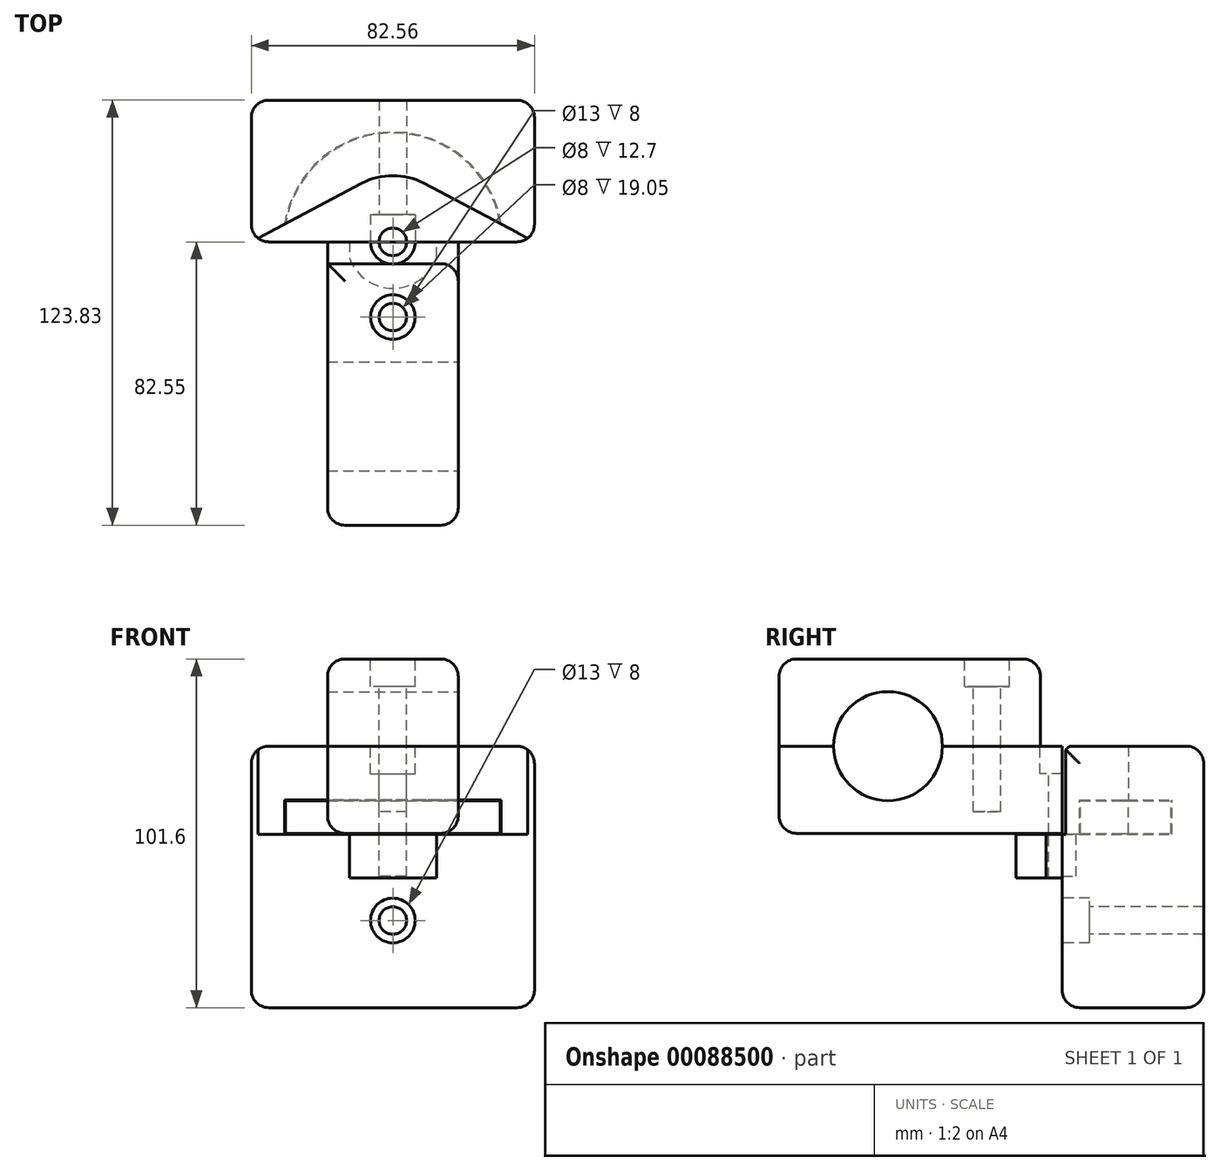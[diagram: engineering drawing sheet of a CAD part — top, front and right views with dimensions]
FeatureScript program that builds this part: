
annotation { "Feature Type Name" : "Feature", "Feature Type Description" : "" }
export const myFeature = defineFeature(function(context is Context, id is Id, definition is map)
    precondition{}
    {
        {
            var Q0;
            Q0=qCreatedBy(makeId("Top.planeOp"),FACE);
            var sketch = newSketch(context, id + "F0", { "sketchPlane" : qUnion([Q0])});
            skLineSegment(sketch, "E0.bottom", {"start": v(0, 0) * mm, "end": v(38.1, 0) * mm});
            skLineSegment(sketch, "E0.top", {"start": v(0, 82.55) * mm, "end": v(38.1, 82.55) * mm});
            skLineSegment(sketch, "E0.left", {"start": v(0, 0) * mm, "end": v(0, 82.55) * mm});
            skLineSegment(sketch, "E0.right", {"start": v(38.1, 0) * mm, "end": v(38.1, 82.55) * mm});
            skArc(sketch, "E1", {"start": v(38.1, 82.55) * mm, "mid": v(19.05, 101.6) * mm, "end": v(0, 82.55) * mm});
            skSolve(sketch);
        }
        {
            var Q0;
            Q0=makeQuery(id+"F0.imprint","IMPRINT",FACE,{"disambiguationData":[TD([[makeQuery(id+"F0.imprint","IMPRINT",EDGE,{"derivedFrom":sQuery(id+"F0.wireOp",EDGE,"E0.bottom")}),1.0]])]});
            var Q1;
            Q1=makeQuery(id+"F0.imprint","IMPRINT",FACE,{"disambiguationData":[TD([[makeQuery(id+"F0.imprint","IMPRINT",EDGE,{"derivedFrom":sQuery(id+"F0.wireOp",EDGE,"E0.top")}),1.0]])]});
            extrude(context, id + "F1", {"entities" : qUnion([Q0, Q1]), "depth" : 25.4 * mm});
        }
        {
            var Q0;
            Q0=makeQuery(id+"F1.opExtrude","SWEPT_FACE",FACE,{"disambiguationData":[OSD([sQuery(id+"F0.wireOp",EDGE,"E0.right")])]});
            var sketch = newSketch(context, id + "F2", { "sketchPlane" : qUnion([Q0])});
            skCircle(sketch, "E2", {"center": v(31.75, 25.4) * mm, "radius": 15.88 * mm});
            skSolve(sketch);
        }
        {
            var Q0;
            {var subQ0=sQuery(id+"F2.wireOp",EDGE,"E2");var subQ1=makeQuery(id+"F1.opExtrude","CAP_EDGE",EDGE,{"disambiguationData":[OSD([sQuery(id+"F0.wireOp",EDGE,"E0.right")])],"isStart":false});var subQ2=makeQuery(id+"F2.imprint","INTERSECT",VERTEX,{"disambiguationData":[OD(0.0)],"derivedFrom":[subQ1,subQ0]});Q0=makeQuery(id+"F2.imprint","IMPRINT",FACE,{"disambiguationData":[TD([[makeQuery(id+"F2.imprint","IMPRINT",EDGE,{"disambiguationData":[TD([[subQ2,-1.0]])],"derivedFrom":subQ0}),1.0]])]});}
            extrude(context, id + "F3", {"entities" : qUnion([Q0]), "operationType" : NewBodyOperationType.REMOVE, "endBound" : BoundingType.THROUGH_ALL, "oppositeDirection" : true, "depth" : 25.4 * mm});
        }
        {
            var Q0;
            Q0=makeQuery(id+"F1.opExtrude","SWEPT_EDGE",EDGE,{"disambiguationData":[OSD([sQuery(id+"F0.wireOp",EDGE,"E0.top"),sQuery(id+"F0.wireOp",EDGE,"E0.right"),sQuery(id+"F0.wireOp",EDGE,"E1")])]});
            var Q1;
            Q1=makeQuery(id+"F1.opExtrude","SWEPT_EDGE",EDGE,{"disambiguationData":[OSD([sQuery(id+"F0.wireOp",EDGE,"E0.top"),sQuery(id+"F0.wireOp",EDGE,"E0.left"),sQuery(id+"F0.wireOp",EDGE,"E1")])]});
            cPlane(context, id + "F4", {"entities" : qUnion([Q0, Q1]), "cplaneType" : CPlaneType.LINE_ANGLE, "offset" : 152.4 * mm, "angle" : 0 * degree, "width" : 152.4 * mm, "height" : 152.4 * mm});
        }
        {
            var Q0;
            Q0=qCreatedBy(id+"F4.planeOp",FACE);
            var sketch = newSketch(context, id + "F5", { "sketchPlane" : qUnion([Q0])});
            skLineSegment(sketch, "E3.0", {"start": v(-38.1, 25.4) * mm, "end": v(-38.1, 0) * mm});
            skLineSegment(sketch, "E4.bottom", {"start": v(-38.1, 0) * mm, "end": v(-50.8, 0) * mm});
            skLineSegment(sketch, "E4.top", {"start": v(-38.1, 9.53) * mm, "end": v(-50.8, 9.53) * mm});
            skLineSegment(sketch, "E4.left", {"start": v(-38.1, 0) * mm, "end": v(-38.1, 9.53) * mm});
            skLineSegment(sketch, "E4.right", {"start": v(-50.8, 0) * mm, "end": v(-50.8, 9.53) * mm});
            skSolve(sketch);
        }
        {
            var Q0;
            Q0=makeQuery(id+"F5.imprint","IMPRINT",FACE,{"disambiguationData":[TD([[makeQuery(id+"F5.imprint","IMPRINT",EDGE,{"derivedFrom":sQuery(id+"F5.wireOp",EDGE,"E4.bottom")}),-1.0]])]});
            var Q1;
            Q1=makeQuery(id+"F1.opExtrude","CAP_EDGE",EDGE,{"disambiguationData":[OSD([sQuery(id+"F0.wireOp",EDGE,"E1")])],"isStart":false});
            sweep(context, id + "F6", {"operationType" : NewBodyOperationType.ADD, "profiles" : qUnion([Q0]), "path" : qUnion([Q1])});
        }
        {
            var Q0;
            {var subQ0=sQuery(id+"F0.wireOp",EDGE,"E0.left");var subQ1=sQuery(id+"F0.wireOp",EDGE,"E0.right");var subQ2=sQuery(id+"F0.wireOp",EDGE,"E1");Q0=makeQuery(id+"F3.boolean.opBoolean","SPLIT",FACE,{"disambiguationData":[TD([makeQuery(id+"F1.opExtrude","SWEPT_FACE",FACE,{"disambiguationData":[OSD([subQ2])]})])],"derivedFrom":makeQuery(id+"F1.opExtrude","CAP_FACE",FACE,{"disambiguationData":[OSD([sQuery(id+"F0.wireOp",EDGE,"E0.bottom"),subQ0,subQ1,subQ2])],"isStart":false})});}
            var sketch = newSketch(context, id + "F7", { "sketchPlane" : qUnion([Q0])});
            skLineSegment(sketch, "E5.bottom", {"start": v(19.05, 82.55) * mm, "end": v(-22.23, 82.55) * mm});
            skLineSegment(sketch, "E5.top", {"start": v(19.05, 123.83) * mm, "end": v(-22.23, 123.83) * mm});
            skLineSegment(sketch, "E5.left", {"start": v(19.05, 82.55) * mm, "end": v(19.05, 123.83) * mm});
            skLineSegment(sketch, "E5.right", {"start": v(-22.23, 82.55) * mm, "end": v(-22.23, 123.83) * mm});
            skLineSegment(sketch, "E6.MirrorCS", {"start": v(19.05, 123.83) * mm, "end": v(60.32, 123.83) * mm});
            skLineSegment(sketch, "E7.MirrorCS", {"start": v(60.32, 82.55) * mm, "end": v(60.32, 123.83) * mm});
            skLineSegment(sketch, "E8.MirrorCS", {"start": v(19.05, 82.55) * mm, "end": v(60.32, 82.55) * mm});
            skSolve(sketch);
        }
        {
            var Q0;
            {var subQ1=sQuery(id+"F0.wireOp",EDGE,"E1");var subQ3=makeQuery(id+"F1.opExtrude","CAP_EDGE",EDGE,{"disambiguationData":[OSD([subQ1])],"isStart":false});var subQ5=sQuery(id+"F7.wireOp",EDGE,"E5.left");var subQ7=makeQuery(id+"F7.imprint","INTERSECT",VERTEX,{"derivedFrom":[subQ3,subQ5]});Q0=makeQuery(id+"F7.imprint","IMPRINT",FACE,{"disambiguationData":[TD([[makeQuery(id+"F7.imprint","IMPRINT",EDGE,{"disambiguationData":[TD([[subQ7,1.0]])],"derivedFrom":subQ5}),1.0]])]});}
            var Q1;
            {var subQ1=sQuery(id+"F7.wireOp",EDGE,"E5.left");var subQ3=sQuery(id+"F0.wireOp",EDGE,"E1");var subQ4=makeQuery(id+"F1.opExtrude","CAP_EDGE",EDGE,{"disambiguationData":[OSD([subQ3])],"isStart":false});var subQ5=makeQuery(id+"F7.imprint","INTERSECT",VERTEX,{"derivedFrom":[subQ4,subQ1]});Q1=makeQuery(id+"F7.imprint","IMPRINT",FACE,{"disambiguationData":[TD([[makeQuery(id+"F7.imprint","IMPRINT",EDGE,{"disambiguationData":[TD([[subQ5,1.0]])],"derivedFrom":subQ1}),-1.0]])]});}
            var Q2;
            {var subQ6=sQuery(id+"F7.wireOp",EDGE,"E6.MirrorCS");Q2=makeQuery(id+"F7.imprint","IMPRINT",FACE,{"disambiguationData":[TD([[makeQuery(id+"F7.imprint","IMPRINT",EDGE,{"derivedFrom":subQ6}),-1.0]])]});}
            var Q3;
            {var subQ2=sQuery(id+"F7.wireOp",EDGE,"E5.top");Q3=makeQuery(id+"F7.imprint","IMPRINT",FACE,{"disambiguationData":[TD([[makeQuery(id+"F7.imprint","IMPRINT",EDGE,{"derivedFrom":subQ2}),1.0]])]});}
            extrude(context, id + "F8", {"entities" : qUnion([Q0, Q1, Q2, Q3]), "oppositeDirection" : true, "depth" : 76.2 * mm});
        }
        {
            var Q0;
            Q0=makeQuery(id+"F1.opExtrude","SWEPT_BODY",BODY,{"disambiguationData":[OSD([sQuery(id+"F0.wireOp",EDGE,"E0.bottom"),sQuery(id+"F0.wireOp",EDGE,"E0.left"),sQuery(id+"F0.wireOp",EDGE,"E0.right"),sQuery(id+"F0.wireOp",EDGE,"E1")])]});
            var Q1;
            Q1=makeQuery(id+"F8.opExtrude","SWEPT_BODY",BODY,{"disambiguationData":[OSD([sQuery(id+"F7.wireOp",EDGE,"E5.bottom"),sQuery(id+"F7.wireOp",EDGE,"E5.top"),sQuery(id+"F7.wireOp",EDGE,"E5.right"),sQuery(id+"F7.wireOp",EDGE,"E6.MirrorCS"),sQuery(id+"F7.wireOp",EDGE,"E7.MirrorCS"),sQuery(id+"F7.wireOp",EDGE,"E8.MirrorCS")])]});
            booleanBodies(context, id + "F9", {"operationType" : BooleanOperationType.SUBTRACTION, "tools" : qUnion([Q0]), "targets" : qUnion([Q1]), "offset" : true, "offsetAll" : true, "offsetDistance" : 0.25 * mm, "keepTools" : true});
        }
        {
            var Q0;
            Q0=makeQuery(id+"F8.opExtrude","CAP_FACE",FACE,{"disambiguationData":[OSD([sQuery(id+"F7.wireOp",EDGE,"E5.bottom"),sQuery(id+"F7.wireOp",EDGE,"E5.top"),sQuery(id+"F7.wireOp",EDGE,"E5.right"),sQuery(id+"F7.wireOp",EDGE,"E6.MirrorCS"),sQuery(id+"F7.wireOp",EDGE,"E7.MirrorCS"),sQuery(id+"F7.wireOp",EDGE,"E8.MirrorCS")])],"isStart":true});
            var sketch = newSketch(context, id + "F10", { "sketchPlane" : qUnion([Q0])});
            skLineSegment(sketch, "E9", {"start": v(60.32, 82.55) * mm, "end": v(28.08, 99.61) * mm});
            skLineSegment(sketch, "E10", {"start": v(-22.23, 82.55) * mm, "end": v(10.02, 99.61) * mm});
            skLineSegment(sketch, "E11", {"start": v(-22.23, 82.55) * mm, "end": v(60.32, 82.55) * mm});
            skArc(sketch, "E12.0", {"start": v(-0.25, 82.55) * mm, "mid": v(19.05, 101.85) * mm, "end": v(38.35, 82.55) * mm});
            skSolve(sketch);
        }
        {
            var Q0;
            Q0 = qSketchRegion(id + "F10", true);
            var Q1;
            {var subQ0=sQuery(id+"F0.wireOp",EDGE,"E1");Q1=makeQuery(id+"F9.tempBoolean.opBoolean","COPY",FACE,{"derivedFrom":makeQuery(id+"F9.offsetTempBody.opPattern","COPY",FACE,{"derivedFrom":makeQuery(id+"F6.boolean.opBoolean","MERGE",FACE,{"derivedFrom":[makeQuery(id+"F1.opExtrude","CAP_FACE",FACE,{"disambiguationData":[OSD([sQuery(id+"F0.wireOp",EDGE,"E0.bottom"),sQuery(id+"F0.wireOp",EDGE,"E0.left"),sQuery(id+"F0.wireOp",EDGE,"E0.right"),subQ0])],"isStart":true}),makeQuery(id+"F6.opSweep","SWEPT_FACE",FACE,{"disambiguationData":[OSD([subQ0,sQuery(id+"F5.wireOp",EDGE,"E4.bottom")])]})]}),"instanceName":"1"})});}
            extrude(context, id + "F11", {"entities" : qUnion([Q0]), "operationType" : NewBodyOperationType.REMOVE, "endBound" : BoundingType.UP_TO_SURFACE, "oppositeDirection" : true, "endBoundEntityFace" : qUnion([Q1]), "depth" : 25.4 * mm});
        }
        {
            var Q0;
            Q0=makeQuery(id+"F11.boolean.opBoolean","COPY",FACE,{"derivedFrom":makeQuery(id+"F11.opExtrude","SWEPT_FACE",FACE,{"disambiguationData":[OSD([sQuery(id+"F10.wireOp",EDGE,"E9")])]})});
            var sketch = newSketch(context, id + "F12", { "sketchPlane" : qUnion([Q0])});
            skCircle(sketch, "E13", {"center": v(29.03, 25.4) * mm, "radius": 15.88 * mm});
            skSolve(sketch);
        }
        {
            var Q0;
            {var subQ0=sQuery(id+"F12.wireOp",EDGE,"E13");var subQ1=sQuery(id+"F10.wireOp",EDGE,"E9");var subQ5=makeQuery(id+"F11.boolean.opBoolean","COPY",EDGE,{"derivedFrom":makeQuery(id+"F11.opExtrude","CAP_EDGE",EDGE,{"disambiguationData":[OSD([subQ1])],"isStart":true})});var subQ6=makeQuery(id+"F12.imprint","INTERSECT",VERTEX,{"derivedFrom":[subQ5,subQ0]});Q0=makeQuery(id+"F12.imprint","IMPRINT",FACE,{"disambiguationData":[TD([[makeQuery(id+"F12.imprint","IMPRINT",EDGE,{"disambiguationData":[TD([[subQ6,-1.0]])],"derivedFrom":subQ0}),1.0]])]});}
            extrude(context, id + "F13", {"entities" : qUnion([Q0]), "operationType" : NewBodyOperationType.REMOVE, "oppositeDirection" : true, "depth" : 25.4 * mm});
        }
        {
            var Q0;
            Q0=makeQuery(id+"F11.boolean.opBoolean","COPY",FACE,{"derivedFrom":makeQuery(id+"F11.opExtrude","SWEPT_FACE",FACE,{"disambiguationData":[OSD([sQuery(id+"F10.wireOp",EDGE,"E10")])]})});
            var sketch = newSketch(context, id + "F14", { "sketchPlane" : qUnion([Q0])});
            skCircle(sketch, "E14", {"center": v(4.65, 25.4) * mm, "radius": 15.88 * mm});
            skSolve(sketch);
        }
        {
            var Q0;
            {var subQ0=sQuery(id+"F14.wireOp",EDGE,"E14");var subQ1=sQuery(id+"F10.wireOp",EDGE,"E10");var subQ5=makeQuery(id+"F11.boolean.opBoolean","COPY",EDGE,{"derivedFrom":makeQuery(id+"F11.opExtrude","CAP_EDGE",EDGE,{"disambiguationData":[OSD([subQ1])],"isStart":true})});var subQ6=makeQuery(id+"F14.imprint","INTERSECT",VERTEX,{"derivedFrom":[subQ5,subQ0]});Q0=makeQuery(id+"F14.imprint","IMPRINT",FACE,{"disambiguationData":[TD([[makeQuery(id+"F14.imprint","IMPRINT",EDGE,{"disambiguationData":[TD([[subQ6,1.0]])],"derivedFrom":subQ0}),1.0]])]});}
            extrude(context, id + "F15", {"entities" : qUnion([Q0]), "operationType" : NewBodyOperationType.REMOVE, "oppositeDirection" : true, "depth" : 25.4 * mm});
        }
        {
            var Q0;
            Q0=makeQuery(id+"F8.opExtrude","SWEPT_FACE",FACE,{"disambiguationData":[OSD([sQuery(id+"F7.wireOp",EDGE,"E5.bottom"),sQuery(id+"F7.wireOp",EDGE,"E8.MirrorCS")])]});
            var sketch = newSketch(context, id + "F16", { "sketchPlane" : qUnion([Q0])});
            skCircle(sketch, "E15", {"center": v(19.05, -25.4) * mm, "radius": 4 * mm});
            skPoint(sketch, "E15.centerSnap0", {"position": v(19.05, -50.8) * mm});
            skSolve(sketch);
        }
        {
            var Q0;
            Q0=makeQuery(id+"F16.imprint","IMPRINT",FACE,{"disambiguationData":[TD([[makeQuery(id+"F16.imprint","IMPRINT",EDGE,{"derivedFrom":sQuery(id+"F16.wireOp",EDGE,"E15")}),1.0]])]});
            extrude(context, id + "F17", {"entities" : qUnion([Q0]), "operationType" : NewBodyOperationType.REMOVE, "endBound" : BoundingType.THROUGH_ALL, "oppositeDirection" : true, "depth" : 25.4 * mm});
        }
        {
            var Q0;
            Q0=makeQuery(id+"F8.opExtrude","SWEPT_FACE",FACE,{"disambiguationData":[OSD([sQuery(id+"F7.wireOp",EDGE,"E5.bottom"),sQuery(id+"F7.wireOp",EDGE,"E8.MirrorCS")])]});
            var sketch = newSketch(context, id + "F18", { "sketchPlane" : qUnion([Q0])});
            skCircle(sketch, "E16.0", {"center": v(19.05, -25.4) * mm, "radius": 6.5 * mm});
            skSolve(sketch);
        }
        {
            var Q0;
            Q0=makeQuery(id+"F18.imprint","IMPRINT",FACE,{"disambiguationData":[TD([[makeQuery(id+"F18.imprint","IMPRINT",EDGE,{"derivedFrom":sQuery(id+"F18.wireOp",EDGE,"E16.0")}),1.0]])]});
            extrude(context, id + "F19", {"entities" : qUnion([Q0]), "operationType" : NewBodyOperationType.REMOVE, "oppositeDirection" : true, "depth" : 8 * mm});
        }
        {
            var Q0;
            Q0=makeQuery(id+"F1.opExtrude","SWEPT_FACE",FACE,{"disambiguationData":[OSD([sQuery(id+"F0.wireOp",EDGE,"E0.right")])]});
            var sketch = newSketch(context, id + "F20", { "sketchPlane" : qUnion([Q0])});
            skArc(sketch, "E17.0.0", {"start": v(47.62, 25.4) * mm, "mid": v(31.75, 9.53) * mm, "end": v(15.87, 25.4) * mm});
            skLineSegment(sketch, "E17.0.1", {"start": v(15.87, 25.4) * mm, "end": v(0, 25.4) * mm});
            skLineSegment(sketch, "E17.0.2", {"start": v(0, 25.4) * mm, "end": v(0, 0) * mm});
            skLineSegment(sketch, "E17.0.3", {"start": v(0, 0) * mm, "end": v(82.55, 0) * mm});
            skLineSegment(sketch, "E17.0.4", {"start": v(82.55, 0) * mm, "end": v(82.55, 9.53) * mm});
            skLineSegment(sketch, "E17.0.5", {"start": v(82.55, 9.53) * mm, "end": v(82.55, 25.4) * mm});
            skLineSegment(sketch, "E17.0.6", {"start": v(82.55, 25.4) * mm, "end": v(47.62, 25.4) * mm});
            skLineSegment(sketch, "E18.bottom", {"start": v(0, 25.4) * mm, "end": v(76.2, 25.4) * mm});
            skLineSegment(sketch, "E18.top", {"start": v(0, 50.8) * mm, "end": v(76.2, 50.8) * mm});
            skLineSegment(sketch, "E18.left", {"start": v(0, 25.4) * mm, "end": v(0, 50.8) * mm});
            skLineSegment(sketch, "E18.right", {"start": v(76.2, 25.4) * mm, "end": v(76.2, 50.8) * mm});
            skArc(sketch, "E19.MirrorCS", {"start": v(47.62, 25.4) * mm, "mid": v(31.75, 41.28) * mm, "end": v(15.87, 25.4) * mm});
            skSolve(sketch);
        }
        {
            var Q0;
            Q0=makeQuery(id+"F20.imprint","IMPRINT",FACE,{"disambiguationData":[TD([[makeQuery(id+"F20.imprint","IMPRINT",EDGE,{"derivedFrom":sQuery(id+"F20.wireOp",EDGE,"E18.top")}),-1.0]])]});
            var Q1;
            Q1=makeQuery(id+"F1.opExtrude","SWEPT_FACE",FACE,{"disambiguationData":[OSD([sQuery(id+"F0.wireOp",EDGE,"E0.left")])]});
            extrude(context, id + "F21", {"entities" : qUnion([Q0]), "endBound" : BoundingType.UP_TO_SURFACE, "oppositeDirection" : true, "endBoundEntityFace" : qUnion([Q1]), "depth" : 25.4 * mm});
        }
        {
            var Q0;
            Q0=makeQuery(id+"F21.opExtrude","SWEPT_FACE",FACE,{"disambiguationData":[OSD([sQuery(id+"F20.wireOp",EDGE,"E18.top")])]});
            var sketch = newSketch(context, id + "F22", { "sketchPlane" : qUnion([Q0])});
            skCircle(sketch, "E20", {"center": v(19.05, 60.62) * mm, "radius": 4 * mm});
            skSolve(sketch);
        }
        {
            var Q0;
            Q0 = qSketchRegion(id + "F22", true);
            extrude(context, id + "F23", {"entities" : qUnion([Q0]), "operationType" : NewBodyOperationType.REMOVE, "oppositeDirection" : true, "depth" : 44.45 * mm});
        }
        {
            var Q0;
            Q0=makeQuery(id+"F21.opExtrude","SWEPT_EDGE",EDGE,{"disambiguationData":[OSD([sQuery(id+"F20.wireOp",EDGE,"E18.top"),sQuery(id+"F20.wireOp",EDGE,"E18.left")])]});
            var Q1;
            Q1=makeQuery(id+"F21.opExtrude","CAP_EDGE",EDGE,{"disambiguationData":[OSD([sQuery(id+"F20.wireOp",EDGE,"E18.top")])],"isStart":true});
            var Q2;
            Q2=makeQuery(id+"F21.opExtrude","CAP_EDGE",EDGE,{"disambiguationData":[OSD([sQuery(id+"F20.wireOp",EDGE,"E18.top")])],"isStart":false});
            var Q3;
            Q3=makeQuery(id+"F21.opExtrude","CAP_EDGE",EDGE,{"disambiguationData":[OSD([sQuery(id+"F20.wireOp",EDGE,"E18.left")])],"isStart":false});
            var Q4;
            Q4=makeQuery(id+"F1.opExtrude","SWEPT_EDGE",EDGE,{"disambiguationData":[OSD([sQuery(id+"F0.wireOp",EDGE,"E0.bottom"),sQuery(id+"F0.wireOp",EDGE,"E0.left")])]});
            var Q5;
            Q5=makeQuery(id+"F1.opExtrude","SWEPT_EDGE",EDGE,{"disambiguationData":[OSD([sQuery(id+"F0.wireOp",EDGE,"E0.bottom"),sQuery(id+"F0.wireOp",EDGE,"E0.right")])]});
            var Q6;
            Q6=makeQuery(id+"F21.opExtrude","CAP_EDGE",EDGE,{"disambiguationData":[OSD([sQuery(id+"F20.wireOp",EDGE,"E18.left")])],"isStart":true});
            var Q7;
            Q7=makeQuery(id+"F21.opExtrude","CAP_EDGE",EDGE,{"disambiguationData":[OSD([sQuery(id+"F20.wireOp",EDGE,"E18.right")])],"isStart":true});
            var Q8;
            Q8=makeQuery(id+"F21.opExtrude","SWEPT_EDGE",EDGE,{"disambiguationData":[OSD([sQuery(id+"F20.wireOp",EDGE,"E18.top"),sQuery(id+"F20.wireOp",EDGE,"E18.right")])]});
            var Q9;
            Q9=makeQuery(id+"F1.opExtrude","CAP_EDGE",EDGE,{"disambiguationData":[OSD([sQuery(id+"F0.wireOp",EDGE,"E0.bottom")])],"isStart":true});
            var Q10;
            Q10=makeQuery(id+"F1.opExtrude","CAP_EDGE",EDGE,{"disambiguationData":[OSD([sQuery(id+"F0.wireOp",EDGE,"E0.right")])],"isStart":true});
            var Q11;
            Q11=makeQuery(id+"F1.opExtrude","CAP_EDGE",EDGE,{"disambiguationData":[OSD([sQuery(id+"F0.wireOp",EDGE,"E0.left")])],"isStart":true});
            var Q12;
            Q12=makeQuery(id+"F8.opExtrude","CAP_EDGE",EDGE,{"disambiguationData":[OSD([sQuery(id+"F7.wireOp",EDGE,"E5.right")])],"isStart":true});
            var Q13;
            Q13=makeQuery(id+"F8.opExtrude","SWEPT_EDGE",EDGE,{"disambiguationData":[OSD([sQuery(id+"F7.wireOp",EDGE,"E5.top"),sQuery(id+"F7.wireOp",EDGE,"E5.right")])]});
            var Q14;
            Q14=makeQuery(id+"F8.opExtrude","CAP_EDGE",EDGE,{"disambiguationData":[OSD([sQuery(id+"F7.wireOp",EDGE,"E5.right")])],"isStart":false});
            var Q15;
            Q15=makeQuery(id+"F11.boolean.opBoolean","SPLIT",EDGE,{"derivedFrom":makeQuery(id+"F8.opExtrude","SWEPT_EDGE",EDGE,{"disambiguationData":[OSD([sQuery(id+"F7.wireOp",EDGE,"E5.bottom"),sQuery(id+"F7.wireOp",EDGE,"E5.right")])]})});
            var Q16;
            Q16=makeQuery(id+"F8.opExtrude","CAP_EDGE",EDGE,{"disambiguationData":[OSD([sQuery(id+"F7.wireOp",EDGE,"E5.bottom"),sQuery(id+"F7.wireOp",EDGE,"E8.MirrorCS")])],"isStart":false});
            var Q17;
            Q17=makeQuery(id+"F8.opExtrude","CAP_EDGE",EDGE,{"disambiguationData":[OSD([sQuery(id+"F7.wireOp",EDGE,"E5.top"),sQuery(id+"F7.wireOp",EDGE,"E6.MirrorCS")])],"isStart":true});
            var Q18;
            Q18=makeQuery(id+"F11.boolean.opBoolean","SPLIT",EDGE,{"derivedFrom":makeQuery(id+"F8.opExtrude","SWEPT_EDGE",EDGE,{"disambiguationData":[OSD([sQuery(id+"F7.wireOp",EDGE,"E7.MirrorCS"),sQuery(id+"F7.wireOp",EDGE,"E8.MirrorCS")])]})});
            var Q19;
            Q19=makeQuery(id+"F8.opExtrude","CAP_EDGE",EDGE,{"disambiguationData":[OSD([sQuery(id+"F7.wireOp",EDGE,"E7.MirrorCS")])],"isStart":false});
            var Q20;
            Q20=makeQuery(id+"F8.opExtrude","SWEPT_EDGE",EDGE,{"disambiguationData":[OSD([sQuery(id+"F7.wireOp",EDGE,"E6.MirrorCS"),sQuery(id+"F7.wireOp",EDGE,"E7.MirrorCS")])]});
            var Q21;
            Q21=makeQuery(id+"F8.opExtrude","CAP_EDGE",EDGE,{"disambiguationData":[OSD([sQuery(id+"F7.wireOp",EDGE,"E5.top"),sQuery(id+"F7.wireOp",EDGE,"E6.MirrorCS")])],"isStart":false});
            var Q22;
            Q22=makeQuery(id+"F8.opExtrude","CAP_EDGE",EDGE,{"disambiguationData":[OSD([sQuery(id+"F7.wireOp",EDGE,"E7.MirrorCS")])],"isStart":true});
            fillet(context, id + "F24", {"entities" : qUnion([Q0, Q1, Q2, Q3, Q4, Q5, Q6, Q7, Q8, Q9, Q10, Q11, Q12, Q13, Q14, Q15, Q16, Q17, Q18, Q19, Q20, Q21, Q22]), "radius" : 5.08 * mm, "allowEdgeOverflow" : false});
        }
        {
            var Q0;
            {var subQ0=sQuery(id+"F0.wireOp",EDGE,"E0.left");var subQ1=sQuery(id+"F0.wireOp",EDGE,"E0.right");var subQ2=sQuery(id+"F0.wireOp",EDGE,"E1");Q0=makeQuery(id+"F3.boolean.opBoolean","SPLIT",FACE,{"disambiguationData":[TD([makeQuery(id+"F1.opExtrude","SWEPT_FACE",FACE,{"disambiguationData":[OSD([subQ2])]})])],"derivedFrom":makeQuery(id+"F1.opExtrude","CAP_FACE",FACE,{"disambiguationData":[OSD([sQuery(id+"F0.wireOp",EDGE,"E0.bottom"),subQ0,subQ1,subQ2])],"isStart":false})});}
            var sketch = newSketch(context, id + "F25", { "sketchPlane" : qUnion([Q0])});
            skCircle(sketch, "E21", {"center": v(19.05, 82.55) * mm, "radius": 4 * mm});
            skPoint(sketch, "E22", {"position": v(19.05, 101.6) * mm});
            skSolve(sketch);
        }
        {
            var Q0;
            Q0 = qSketchRegion(id + "F25", true);
            extrude(context, id + "F26", {"entities" : qUnion([Q0]), "operationType" : NewBodyOperationType.REMOVE, "oppositeDirection" : true, "depth" : 37.95 * mm});
        }
        {
            var Q0;
            Q0=makeQuery(id+"F21.opExtrude","SWEPT_FACE",FACE,{"disambiguationData":[OSD([sQuery(id+"F20.wireOp",EDGE,"E18.top")])]});
            var sketch = newSketch(context, id + "F27", { "sketchPlane" : qUnion([Q0])});
            skCircle(sketch, "E23", {"center": v(19.05, 60.62) * mm, "radius": 6.5 * mm});
            skSolve(sketch);
        }
        {
            var Q0;
            Q0 = qSketchRegion(id + "F27", true);
            extrude(context, id + "F28", {"entities" : qUnion([Q0]), "operationType" : NewBodyOperationType.REMOVE, "oppositeDirection" : true, "depth" : 8 * mm});
        }
        {
            var Q0;
            {var subQ0=sQuery(id+"F0.wireOp",EDGE,"E1");Q0=makeQuery(id+"F11.boolean.opBoolean","MERGE",FACE,{"derivedFrom":[makeQuery(id+"F9.tempBoolean.opBoolean","COPY",FACE,{"derivedFrom":makeQuery(id+"F9.offsetTempBody.opPattern","COPY",FACE,{"derivedFrom":makeQuery(id+"F6.boolean.opBoolean","MERGE",FACE,{"derivedFrom":[makeQuery(id+"F1.opExtrude","CAP_FACE",FACE,{"disambiguationData":[OSD([sQuery(id+"F0.wireOp",EDGE,"E0.bottom"),sQuery(id+"F0.wireOp",EDGE,"E0.left"),sQuery(id+"F0.wireOp",EDGE,"E0.right"),subQ0])],"isStart":true}),makeQuery(id+"F6.opSweep","SWEPT_FACE",FACE,{"disambiguationData":[OSD([subQ0,sQuery(id+"F5.wireOp",EDGE,"E4.bottom")])]})]}),"instanceName":"1"})})],"fromTools":[makeQuery(id+"F11.opExtrude","CAP_FACE",FACE,{"disambiguationData":[OSD([sQuery(id+"F10.wireOp",EDGE,"E9"),sQuery(id+"F10.wireOp",EDGE,"E10"),sQuery(id+"F10.wireOp",EDGE,"E11"),sQuery(id+"F10.wireOp",EDGE,"E12.0")])],"isStart":false})]});}
            var sketch = newSketch(context, id + "F29", { "sketchPlane" : qUnion([Q0])});
            skCircle(sketch, "E24.0", {"center": v(19.05, 82.55) * mm, "radius": 4 * mm});
            skCircle(sketch, "E25.0", {"center": v(19.05, 82.55) * mm, "radius": 13.53 * mm});
            skLineSegment(sketch, "E26.0", {"start": v(6.35, 82.55) * mm, "end": v(6.35, 53.97) * mm});
            skArc(sketch, "E26.1", {"start": v(31.75, 82.55) * mm, "mid": v(19.05, 95.25) * mm, "end": v(6.35, 82.55) * mm});
            skLineSegment(sketch, "E26.2", {"start": v(31.75, 53.98) * mm, "end": v(31.75, 82.55) * mm});
            skLineSegment(sketch, "E26.3", {"start": v(6.35, 53.97) * mm, "end": v(31.75, 53.98) * mm});
            skSolve(sketch);
        }
        {
            var Q0;
            {var subQ15=sQuery(id+"F29.wireOp",EDGE,"E25.0");var subQ17=sQuery(id+"F29.wireOp",EDGE,"E26.0");var subQ21=makeQuery(id+"F29.imprint","INTERSECT",VERTEX,{"derivedFrom":[subQ15,subQ17]});Q0=makeQuery(id+"F29.imprint","IMPRINT",FACE,{"disambiguationData":[TD([[makeQuery(id+"F29.imprint","IMPRINT",EDGE,{"disambiguationData":[TD([[subQ21,-1.0]])],"derivedFrom":subQ15}),1.0]])]});}
            extrude(context, id + "F30", {"entities" : qUnion([Q0]), "operationType" : NewBodyOperationType.ADD, "oppositeDirection" : true, "depth" : 12.7 * mm});
        }
        {
            var Q0;
            {var subQ0=sQuery(id+"F0.wireOp",EDGE,"E0.left");var subQ1=sQuery(id+"F0.wireOp",EDGE,"E0.right");var subQ2=sQuery(id+"F0.wireOp",EDGE,"E1");Q0=makeQuery(id+"F3.boolean.opBoolean","SPLIT",FACE,{"disambiguationData":[TD([makeQuery(id+"F1.opExtrude","SWEPT_FACE",FACE,{"disambiguationData":[OSD([subQ2])]})])],"derivedFrom":makeQuery(id+"F1.opExtrude","CAP_FACE",FACE,{"disambiguationData":[OSD([sQuery(id+"F0.wireOp",EDGE,"E0.bottom"),subQ0,subQ1,subQ2])],"isStart":false})});}
            var sketch = newSketch(context, id + "F31", { "sketchPlane" : qUnion([Q0])});
            skCircle(sketch, "E27", {"center": v(19.05, 82.55) * mm, "radius": 6.5 * mm});
            skSolve(sketch);
        }
        {
            var Q0;
            Q0 = qSketchRegion(id + "F31", true);
            extrude(context, id + "F32", {"entities" : qUnion([Q0]), "operationType" : NewBodyOperationType.REMOVE, "oppositeDirection" : true, "depth" : 8 * mm});
        }
    });
